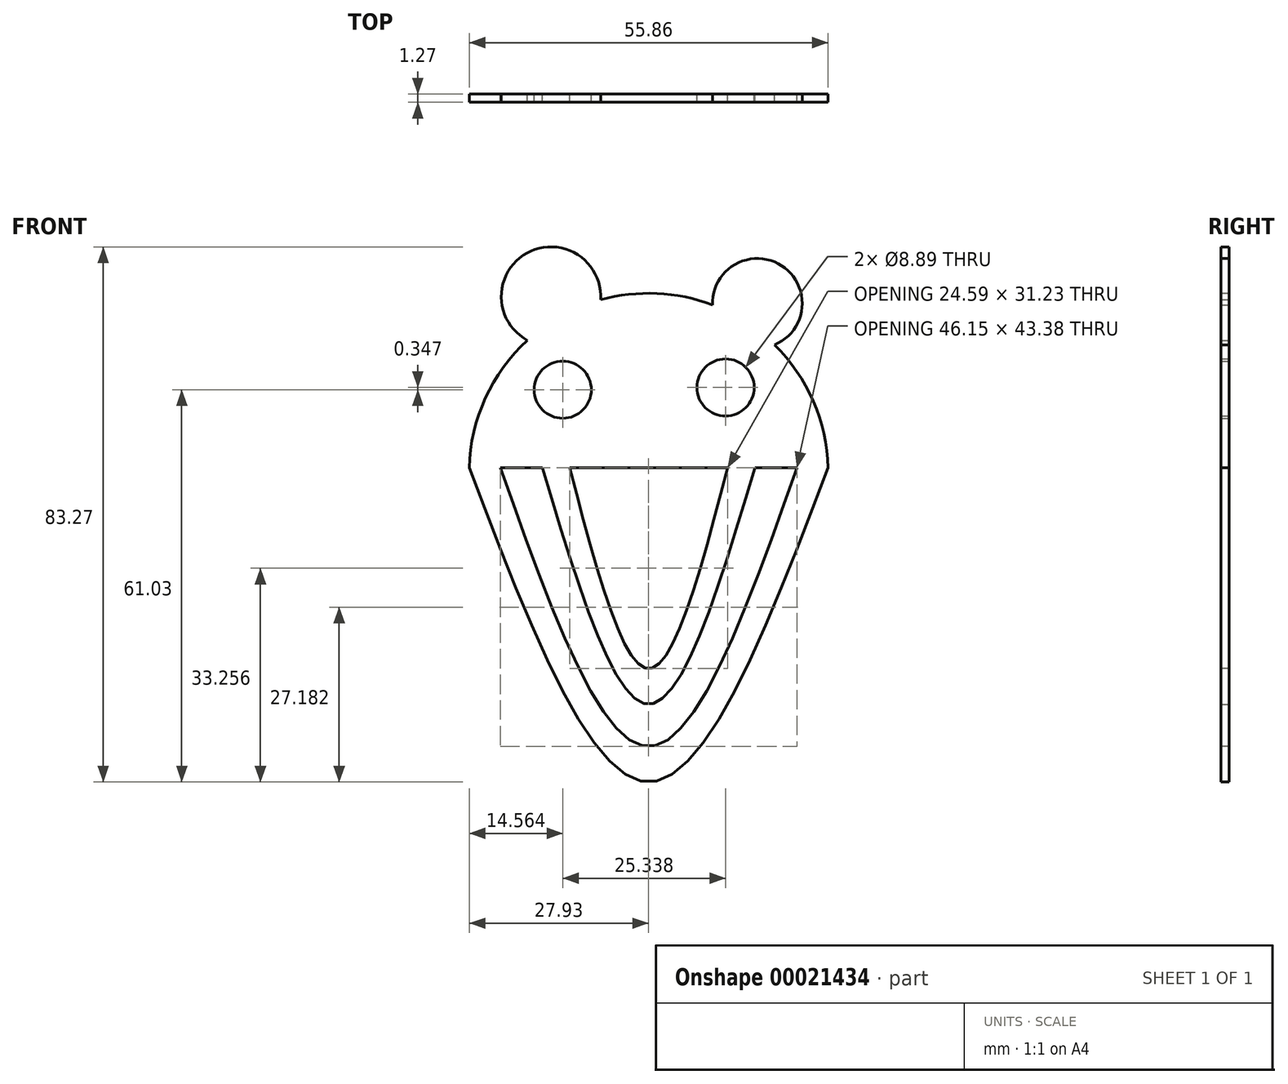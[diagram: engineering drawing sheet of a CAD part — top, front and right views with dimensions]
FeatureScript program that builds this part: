
annotation { "Feature Type Name" : "Feature", "Feature Type Description" : "" }
export const myFeature = defineFeature(function(context is Context, id is Id, definition is map)
    precondition{}
    {
        {
            var Q0;
            Q0=qCreatedBy(makeId("Front.planeOp"),FACE);
            var sketch = newSketch(context, id + "F0", { "sketchPlane" : qUnion([Q0])});
            skFitSpline(sketch, "E0", {"points": [v(-27.93, 0) * mm, v(0, -48.87) * mm, v(27.93, 0) * mm], "startDerivative": vector(55.85, -146.6) * mm, "endDerivative": vector(55.85, 146.6) * mm});
            skLineSegment(sketch, "E1", {"start": v(-23.08, 0) * mm, "end": v(-16.53, 0) * mm});
            skFitSpline(sketch, "E2", {"points": [v(-23.08, 0) * mm, v(0, -43.38) * mm, v(23.08, 0) * mm], "startDerivative": vector(46.15, -130.13) * mm, "endDerivative": vector(46.15, 130.13) * mm});
            skFitSpline(sketch, "E3", {"points": [v(-16.53, 0) * mm, v(0, -36.78) * mm, v(16.53, 0) * mm], "startDerivative": vector(33.06, -110.34) * mm, "endDerivative": vector(33.06, 110.34) * mm});
            skFitSpline(sketch, "E4", {"points": [v(-12.3, 0) * mm, v(0, -31.23) * mm, v(12.3, 0) * mm], "startDerivative": vector(24.6, -93.68) * mm, "endDerivative": vector(24.6, 93.68) * mm});
            skArc(sketch, "E5", {"start": v(27.93, 0) * mm, "mid": v(0, 27.17) * mm, "end": v(-27.93, 0) * mm});
            skLineSegment(sketch, "E6.trimOffspring", {"start": v(-12.3, 0) * mm, "end": v(12.3, 0) * mm});
            skLineSegment(sketch, "E7.trimOffspring", {"start": v(16.53, 0) * mm, "end": v(23.08, 0) * mm});
            skCircle(sketch, "E8", {"center": v(-13.37, 12.16) * mm, "radius": 4.45 * mm});
            skCircle(sketch, "E9", {"center": v(11.97, 12.5) * mm, "radius": 4.45 * mm});
            skArc(sketch, "E10", {"start": v(-7.48, 26.15) * mm, "mid": v(-18.95, 33.43) * mm, "end": v(-18.86, 19.85) * mm});
            skArc(sketch, "E11", {"start": v(19.6, 19.14) * mm, "mid": v(20.69, 31.48) * mm, "end": v(9.92, 25.35) * mm});
            skSolve(sketch);
        }
        {
            var Q0;
            Q0 = qSketchRegion(id + "F0", true);
            extrude(context, id + "F1", {"entities" : qUnion([Q0]), "depth" : 1.27 * mm});
        }
    });
